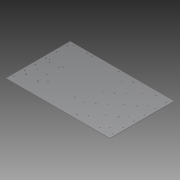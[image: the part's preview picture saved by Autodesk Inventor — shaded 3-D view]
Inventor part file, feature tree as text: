
AUTODESK INVENTOR PART (.ipt)
format: ipt  version: 2013 (Build 170138000, 138)  size: 186,368 bytes
history: native  units: in
note: dims shown in document units (in); Inventor stores cm internally (conversion verified against a paired STEP export)
features: extrude x1, sketch x1
ambient origin geometry x8: Origin, YZ Plane, XZ Plane, XY Plane, X Axis, Y Axis, Z Axis, Center Point
bodies: Solid1 (feature_tree)
feature tree (2):
  extrude  "Extrusion1"  Depth=19.4375in
  sketch  "Sketch1"  dims[d0=12.0in d4=19.4375in d6=0.15in d7=0.15in d8=1.646in d9=2.446in d11=0.1875in d12=0.1875in d13=0.1875in d14=0.1875in d15=1.5in d16=1.5in d17=8.25in d18=5.0in d19=0.2in d20=4.5in d21=0.375in d22=0.7874in d24=4.0in d25=1.1811in d27=3.5in d30=0.125in d31=0.0in d32=0.5in d33=0.2in d34=1.0in d35=0.5in d37=1.0in d38=0.3937in d40=1.0in d41=2.3622in d43=2.0in d45=3.5in d46=0.2in d47=0.7874in d49=4.25in d50=0.7874in d52=7.0in d55=0.7395in d56=0.7395in d57=2.2032in d58=0.26in d59=9.5in d63=0.2in d67=6.5in d68=1.25in d69=2.29in d70=1.75in d71=1.0in d72=2.125in d73=0.7874in d75=2.5in d76=0.7874in d78=4.5in d81=0.2in d82=4.875in d83=1.0in]
